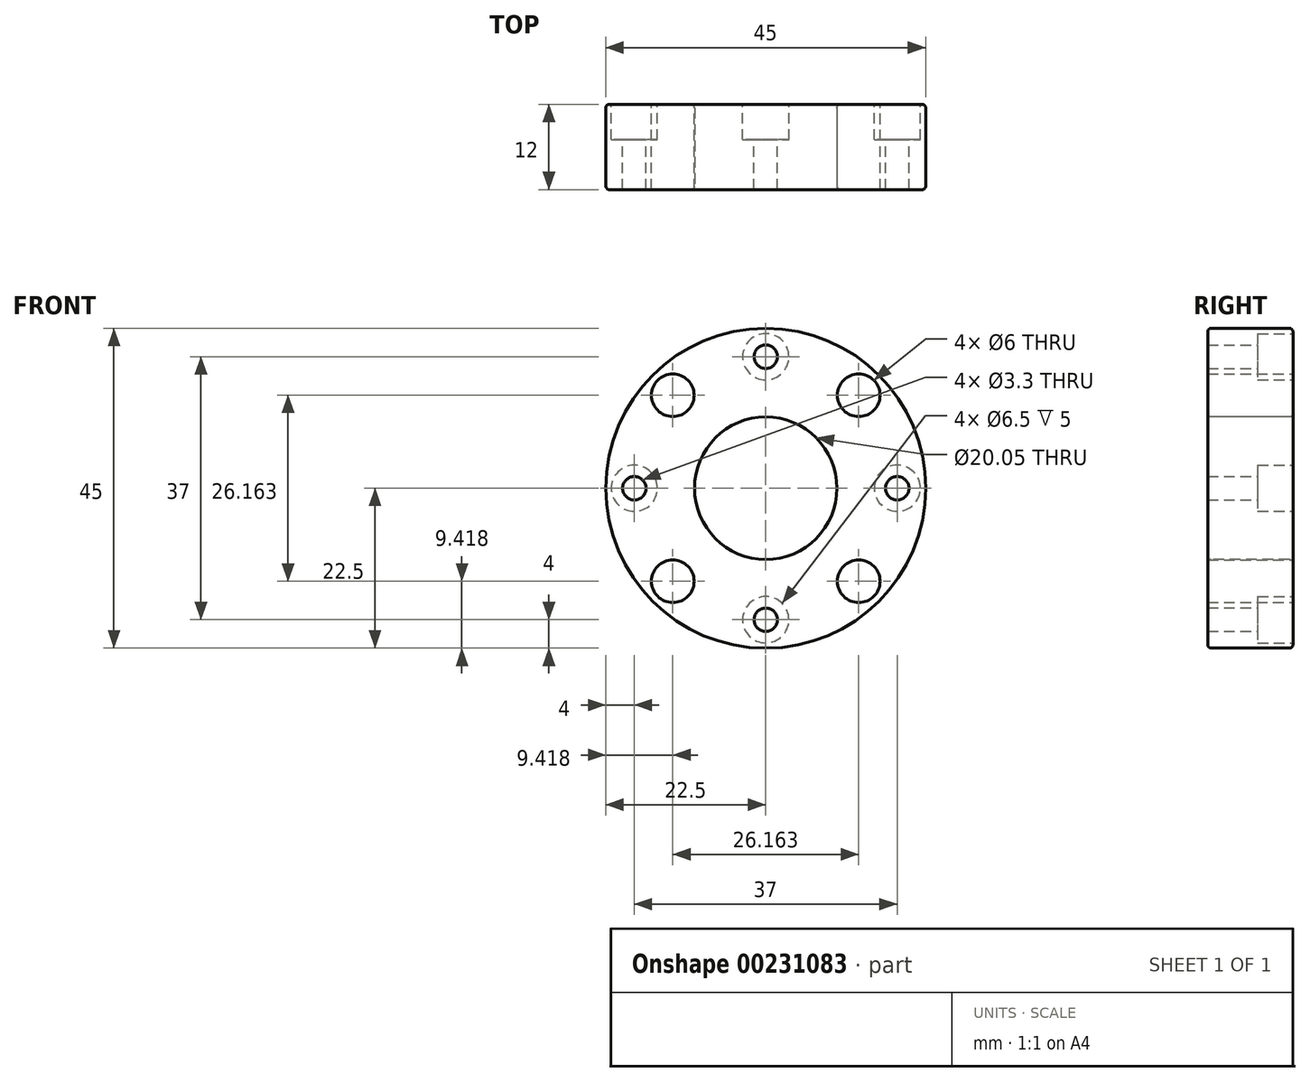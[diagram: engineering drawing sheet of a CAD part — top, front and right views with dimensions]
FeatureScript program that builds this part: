
annotation { "Feature Type Name" : "Feature", "Feature Type Description" : "" }
export const myFeature = defineFeature(function(context is Context, id is Id, definition is map)
    precondition{}
    {
        {
            var Q0;
            Q0=qCreatedBy(makeId("Right.planeOp"),FACE);
            var sketch = newSketch(context, id + "F0", { "sketchPlane" : qUnion([Q0])});
            skLineSegment(sketch, "E0.bottom", {"start": v(-6, 22.5) * mm, "end": v(6, 22.5) * mm});
            skLineSegment(sketch, "E0.top", {"start": v(-6, 10.02) * mm, "end": v(6, 10.02) * mm});
            skLineSegment(sketch, "E0.left", {"start": v(-6, 22.5) * mm, "end": v(-6, 10.02) * mm});
            skLineSegment(sketch, "E0.right", {"start": v(6, 22.5) * mm, "end": v(6, 10.02) * mm});
            skPoint(sketch, "E0.middle", {"position": v(0, 16.26) * mm});
            skLineSegment(sketch, "E1", {"start": v(-4.57, 0) * mm, "end": v(8.33, 0) * mm});
            skSolve(sketch);
        }
        {
            var Q0;
            Q0=makeQuery(id+"F0.imprint","IMPRINT",FACE,{"disambiguationData":[TD([[makeQuery(id+"F0.imprint","IMPRINT",EDGE,{"derivedFrom":sQuery(id+"F0.wireOp",EDGE,"E0.bottom")}),-1.0]])]});
            var Q1;
            Q1=sQuery(id+"F0.wireOp",EDGE,"E1");
            revolve(context, id + "F1", {"entities" : qUnion([Q0]), "axis" : qUnion([Q1]), "revolveType" : RevolveType.FULL});
        }
        {
            var Q0;
            Q0=makeQuery(id+"F1.opRevolve","SWEPT_FACE",FACE,{"disambiguationData":[OSD([sQuery(id+"F0.wireOp",EDGE,"E0.right")])]});
            var sketch = newSketch(context, id + "F2", { "sketchPlane" : qUnion([Q0])});
            skCircle(sketch, "E2", {"center": v(0, 0) * mm, "radius": 18.5 * mm});
            skLineSegment(sketch, "E3", {"start": v(13.08, 13.08) * mm, "end": v(0, 0) * mm});
            skLineSegment(sketch, "E4", {"start": v(-13.08, -13.08) * mm, "end": v(0, 0) * mm});
            skLineSegment(sketch, "E5", {"start": v(0, 0) * mm, "end": v(-13.08, 13.08) * mm});
            skLineSegment(sketch, "E6", {"start": v(0, 0) * mm, "end": v(13.08, -13.08) * mm});
            skPoint(sketch, "E7", {"position": v(-13.08, 13.08) * mm});
            skPoint(sketch, "E8", {"position": v(13.08, 13.08) * mm});
            skPoint(sketch, "E9", {"position": v(-13.08, -13.08) * mm});
            skPoint(sketch, "E10", {"position": v(13.08, -13.08) * mm});
            skPoint(sketch, "E11", {"position": v(0, 18.5) * mm});
            skPoint(sketch, "E12", {"position": v(-18.5, 0) * mm});
            skPoint(sketch, "E13", {"position": v(18.5, 0) * mm});
            skPoint(sketch, "E14", {"position": v(0, -18.5) * mm});
            skSolve(sketch);
        }
        {
            var Q0;
            Q0=sQuery(id+"F2.wireOp",VERTEX,"E7");
            var Q1;
            Q1=sQuery(id+"F2.wireOp",VERTEX,"E8");
            var Q2;
            Q2=sQuery(id+"F2.wireOp",VERTEX,"E9");
            var Q3;
            Q3=sQuery(id+"F2.wireOp",VERTEX,"E10");
            var Q4;
            Q4=makeQuery(id+"F1.opRevolve","SWEPT_BODY",BODY,{"disambiguationData":[OSD([sQuery(id+"F0.wireOp",EDGE,"E0.bottom"),sQuery(id+"F0.wireOp",EDGE,"E0.top"),sQuery(id+"F0.wireOp",EDGE,"E0.left"),sQuery(id+"F0.wireOp",EDGE,"E0.right")])]});
            hole(context, id + "F3", {"style" : HoleStyle.SIMPLE, "endStyle" : HoleEndStyle.THROUGH, "holeDiameter" : 6 * mm, "startFromSketch" : true, "locations" : qUnion([Q0, Q1, Q2, Q3]), "scope" : qUnion([Q4]), "isTappedThrough" : true});
        }
        {
            var Q0;
            Q0=sQuery(id+"F2.wireOp",VERTEX,"E12");
            var Q1;
            Q1=sQuery(id+"F2.wireOp",VERTEX,"E14");
            var Q2;
            Q2=sQuery(id+"F2.wireOp",VERTEX,"E13");
            var Q3;
            Q3=sQuery(id+"F2.wireOp",VERTEX,"E11");
            var Q4;
            Q4=makeQuery(id+"F1.opRevolve","SWEPT_BODY",BODY,{"disambiguationData":[OSD([sQuery(id+"F0.wireOp",EDGE,"E0.bottom"),sQuery(id+"F0.wireOp",EDGE,"E0.top"),sQuery(id+"F0.wireOp",EDGE,"E0.left"),sQuery(id+"F0.wireOp",EDGE,"E0.right")])]});
            hole(context, id + "F4", {"style" : HoleStyle.C_BORE, "endStyle" : HoleEndStyle.THROUGH, "holeDiameter" : 3.3 * mm, "cBoreDiameter" : 6.5 * mm, "cBoreDepth" : 5 * mm, "startFromSketch" : true, "locations" : qUnion([Q0, Q1, Q2, Q3]), "scope" : qUnion([Q4]), "isTappedThrough" : true});
        }
        {
            var Q0;
            Q0=makeQuery(id+"F1.opRevolve","SWEPT_EDGE",EDGE,{"disambiguationData":[OSD([sQuery(id+"F0.wireOp",EDGE,"E0.bottom"),sQuery(id+"F0.wireOp",EDGE,"E0.right")])]});
            var Q1;
            Q1=makeQuery(id+"F1.opRevolve","SWEPT_EDGE",EDGE,{"disambiguationData":[OSD([sQuery(id+"F0.wireOp",EDGE,"E0.bottom"),sQuery(id+"F0.wireOp",EDGE,"E0.left")])]});
            var Q2;
            Q2=makeQuery(id+"F1.opRevolve","SWEPT_EDGE",EDGE,{"disambiguationData":[OSD([sQuery(id+"F0.wireOp",EDGE,"E0.top"),sQuery(id+"F0.wireOp",EDGE,"E0.right")])]});
            var Q3;
            Q3=makeQuery(id+"F1.opRevolve","SWEPT_FACE",FACE,{"disambiguationData":[OSD([sQuery(id+"F0.wireOp",EDGE,"E0.top")])]});
            fillet(context, id + "F5", {"entities" : qUnion([Q0, Q1, Q2, Q3]), "radius" : 0.5 * mm, "tangentPropagation" : true, "allowEdgeOverflow" : false});
        }
    });
